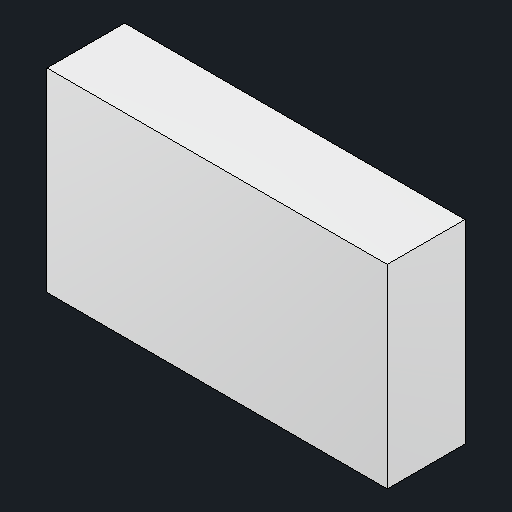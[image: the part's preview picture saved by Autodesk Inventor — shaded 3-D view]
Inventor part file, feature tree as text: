
AUTODESK INVENTOR PART (.ipt)
format: ipt  version: 2023.2 (Build 272271030, 271C)  size: 95,232 bytes
history: native  units: mm
features: extrude x1, sketch x1
ambient origin geometry x8: Origin, YZ Plane, XZ Plane, XY Plane, X Axis, Y Axis, Z Axis, Center Point
bodies: Solid1 (feature_tree)
feature tree (2):
  extrude  "Extrusion1"  Depth=20.0mm
  sketch  "Sketch1"  dims[d0=35.0mm d1=20.0mm d2=8.0mm d3=0.0mm]
